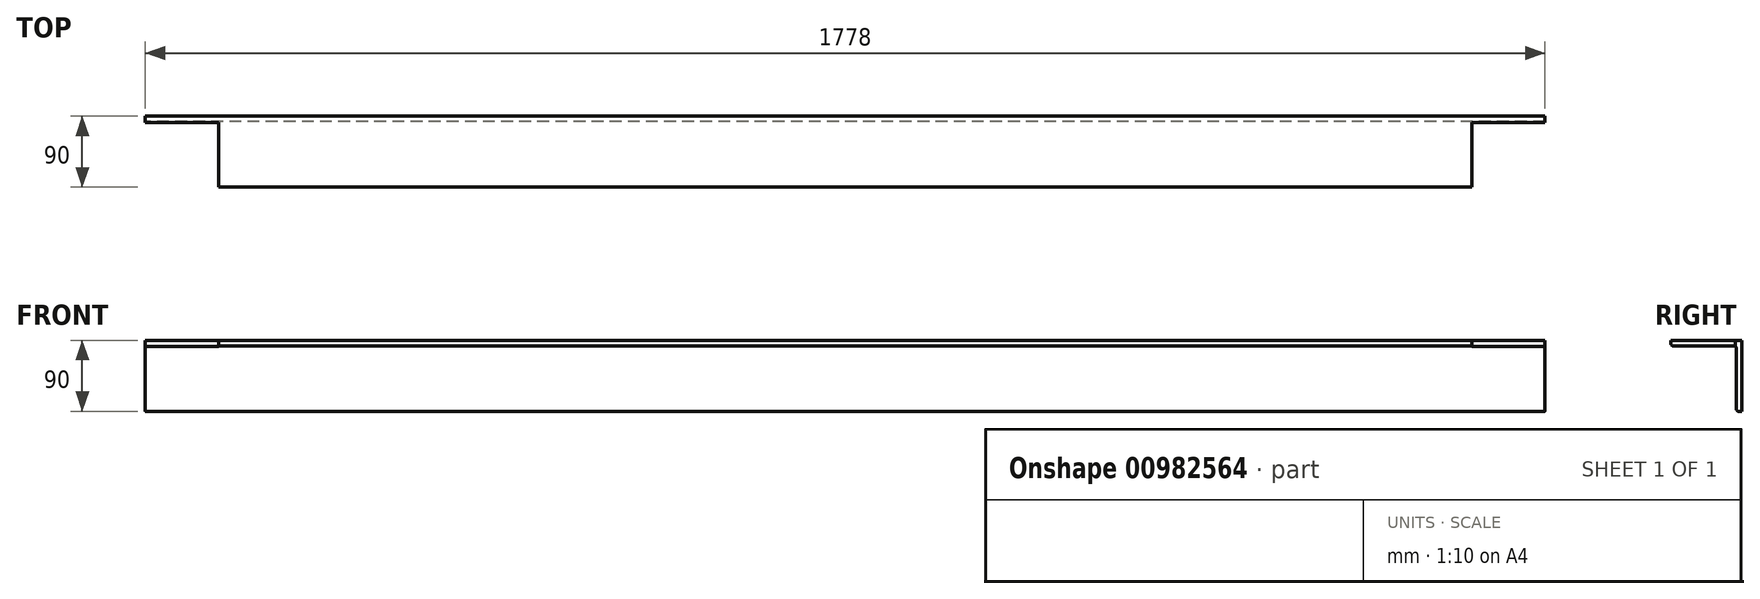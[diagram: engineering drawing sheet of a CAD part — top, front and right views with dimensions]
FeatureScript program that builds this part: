
annotation { "Feature Type Name" : "Feature", "Feature Type Description" : "" }
export const myFeature = defineFeature(function(context is Context, id is Id, definition is map)
    precondition{}
    {
        {
            var Q0;
            Q0=qCreatedBy(makeId("Right.planeOp"),FACE);
            var sketch = newSketch(context, id + "F0", { "sketchPlane" : qUnion([Q0])});
            skLineSegment(sketch, "E0", {"start": v(0, 0) * mm, "end": v(-90, 0) * mm});
            skLineSegment(sketch, "E1", {"start": v(-90, 0) * mm, "end": v(-90, -4) * mm});
            skLineSegment(sketch, "E2", {"start": v(-87, -7) * mm, "end": v(-10, -7) * mm});
            skLineSegment(sketch, "E3", {"start": v(-7, -10) * mm, "end": v(-7, -87) * mm});
            skLineSegment(sketch, "E4", {"start": v(-4, -90) * mm, "end": v(0, -90) * mm});
            skLineSegment(sketch, "E5", {"start": v(0, -90) * mm, "end": v(0, 0) * mm});
            skPoint(sketch, "E6.visualSharp", {"position": v(-90, -7) * mm});
            skArc(sketch, "E6.filletArc", {"start": v(-90, -4) * mm, "mid": v(-89.12, -6.12) * mm, "end": v(-87, -7) * mm});
            skPoint(sketch, "E7.visualSharp", {"position": v(-7, -7) * mm});
            skArc(sketch, "E7.filletArc", {"start": v(-7, -10) * mm, "mid": v(-7.88, -7.88) * mm, "end": v(-10, -7) * mm});
            skPoint(sketch, "E8.visualSharp", {"position": v(-7, -90) * mm});
            skArc(sketch, "E8.filletArc", {"start": v(-7, -87) * mm, "mid": v(-6.12, -89.12) * mm, "end": v(-4, -90) * mm});
            skSolve(sketch);
        }
        {
            var Q0;
            Q0=makeQuery(id+"F0.imprint","IMPRINT",FACE,{"disambiguationData":[TD([[makeQuery(id+"F0.imprint","IMPRINT",EDGE,{"derivedFrom":sQuery(id+"F0.wireOp",EDGE,"E0")}),1.0]])]});
            extrude(context, id + "F1", {"entities" : qUnion([Q0]), "endBound" : BoundingType.SYMMETRIC, "depth" : 1778 * mm, "offsetDistance" : 25 * mm});
        }
        {
            var Q0;
            Q0=makeQuery(id+"F1.opExtrude","SWEPT_FACE",FACE,{"disambiguationData":[OSD([sQuery(id+"F0.wireOp",EDGE,"E0")])]});
            var sketch = newSketch(context, id + "F2", { "sketchPlane" : qUnion([Q0])});
            skLineSegment(sketch, "E9.bottom", {"start": v(796, -90) * mm, "end": v(889, -90) * mm});
            skLineSegment(sketch, "E9.top", {"start": v(796, -8) * mm, "end": v(889, -8) * mm});
            skLineSegment(sketch, "E9.left", {"start": v(796, -90) * mm, "end": v(796, -8) * mm});
            skLineSegment(sketch, "E9.right", {"start": v(889, -90) * mm, "end": v(889, -8) * mm});
            skLineSegment(sketch, "E10.bottom", {"start": v(-889, -90) * mm, "end": v(-796, -90) * mm});
            skLineSegment(sketch, "E10.top", {"start": v(-889, -8) * mm, "end": v(-796, -8) * mm});
            skLineSegment(sketch, "E10.left", {"start": v(-889, -90) * mm, "end": v(-889, -8) * mm});
            skLineSegment(sketch, "E10.right", {"start": v(-796, -90) * mm, "end": v(-796, -8) * mm});
            skSolve(sketch);
        }
        {
            var Q0;
            Q0=makeQuery(id+"F2.imprint","IMPRINT",FACE,{"disambiguationData":[TD([[makeQuery(id+"F2.imprint","IMPRINT",EDGE,{"derivedFrom":sQuery(id+"F2.wireOp",EDGE,"E9.bottom")}),-1.0]])]});
            var Q1;
            Q1=makeQuery(id+"F2.imprint","IMPRINT",FACE,{"disambiguationData":[TD([[makeQuery(id+"F2.imprint","IMPRINT",EDGE,{"derivedFrom":sQuery(id+"F2.wireOp",EDGE,"E10.bottom")}),-1.0]])]});
            extrude(context, id + "F3", {"entities" : qUnion([Q0, Q1]), "operationType" : NewBodyOperationType.REMOVE, "oppositeDirection" : true, "depth" : 25 * mm, "offsetDistance" : 25 * mm});
        }
    });
